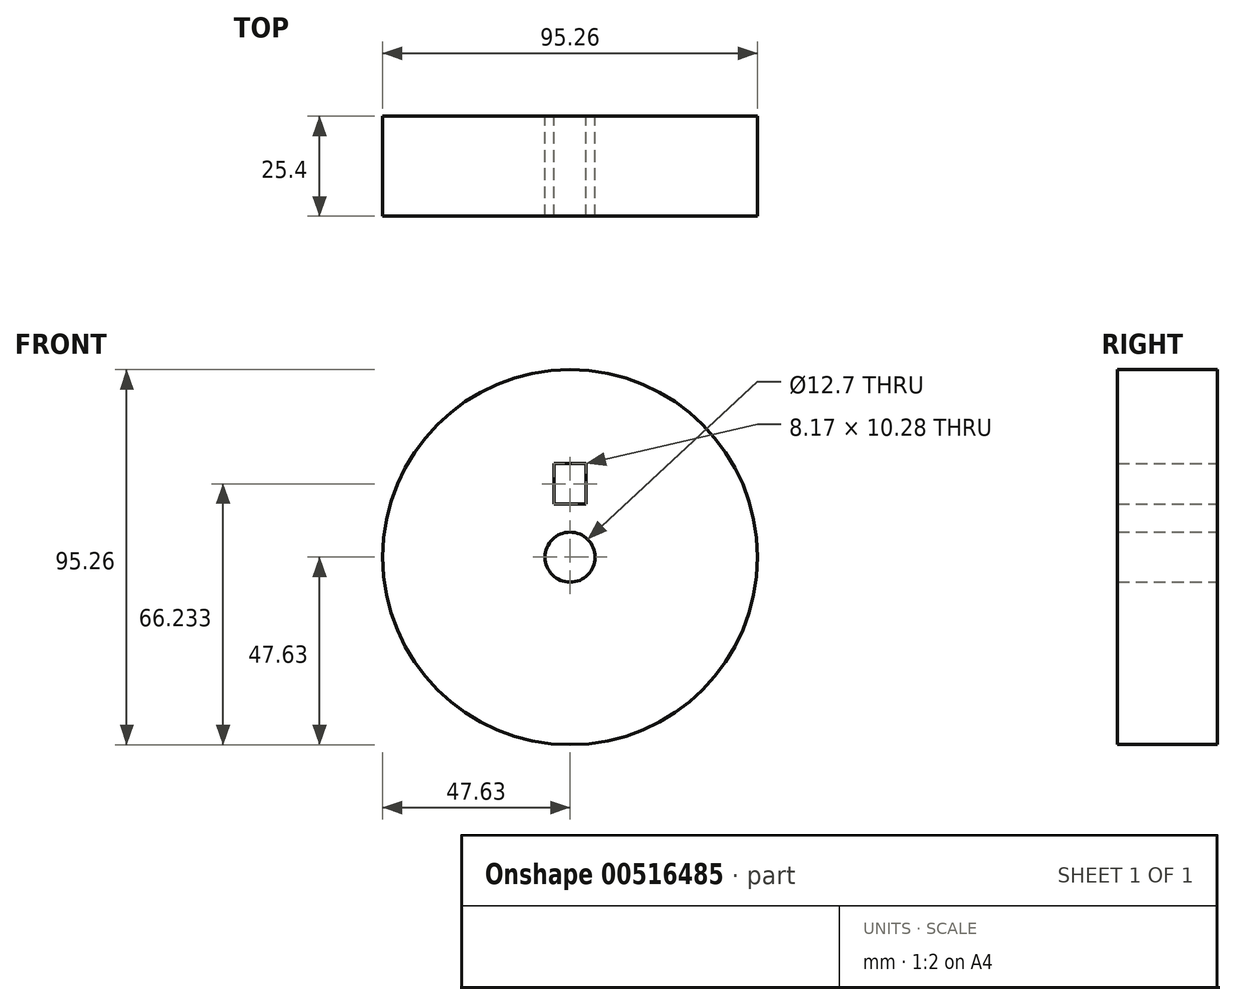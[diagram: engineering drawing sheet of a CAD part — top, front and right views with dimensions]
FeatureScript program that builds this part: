
annotation { "Feature Type Name" : "Feature", "Feature Type Description" : "" }
export const myFeature = defineFeature(function(context is Context, id is Id, definition is map)
    precondition{}
    {
        {
            var Q0;
            Q0=qCreatedBy(makeId("Front.planeOp"),FACE);
            var sketch = newSketch(context, id + "F0", { "sketchPlane" : qUnion([Q0])});
            skCircle(sketch, "E0", {"center": v(0, 0) * mm, "radius": 47.63 * mm});
            skCircle(sketch, "E1", {"center": v(0, 0) * mm, "radius": 6.35 * mm});
            skLineSegment(sketch, "E2.bottom", {"start": v(4.08, 13.46) * mm, "end": v(-4.08, 13.46) * mm});
            skLineSegment(sketch, "E2.top", {"start": v(4.08, 23.75) * mm, "end": v(-4.08, 23.75) * mm});
            skLineSegment(sketch, "E2.left", {"start": v(4.08, 13.46) * mm, "end": v(4.08, 23.75) * mm});
            skLineSegment(sketch, "E2.right", {"start": v(-4.08, 13.46) * mm, "end": v(-4.08, 23.75) * mm});
            skPoint(sketch, "E2.middle", {"position": v(0, 18.6) * mm});
            skSolve(sketch);
        }
        {
            var Q0;
            Q0=makeQuery(id+"F0.imprint","IMPRINT",FACE,{"disambiguationData":[TD([[makeQuery(id+"F0.imprint","IMPRINT",EDGE,{"derivedFrom":sQuery(id+"F0.wireOp",EDGE,"E0")}),1.0]])]});
            extrude(context, id + "F1", {"entities" : qUnion([Q0]), "depth" : 25.4 * mm, "offsetDistance" : 25.4 * mm});
        }
    });
